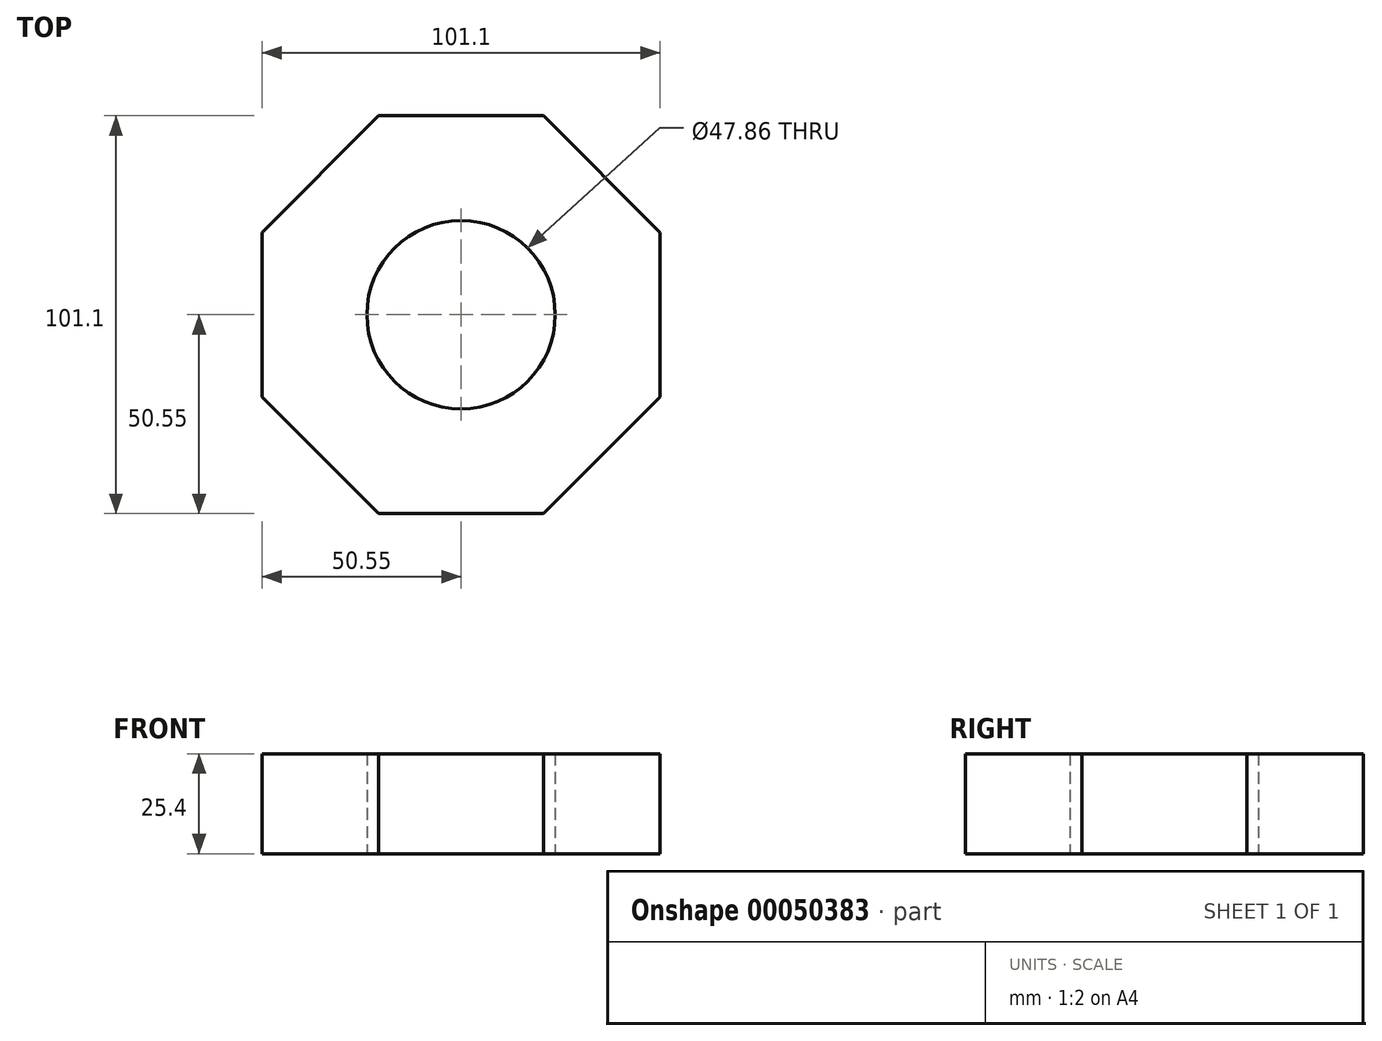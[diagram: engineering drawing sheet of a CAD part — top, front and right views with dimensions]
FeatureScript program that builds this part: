
annotation { "Feature Type Name" : "Feature", "Feature Type Description" : "" }
export const myFeature = defineFeature(function(context is Context, id is Id, definition is map)
    precondition{}
    {
        {
            var Q0;
            Q0=qCreatedBy(makeId("Top.planeOp"),FACE);
            var sketch = newSketch(context, id + "F0", { "sketchPlane" : qUnion([Q0])});
            skCircle(sketch, "E0.cCircle", {"center": v(0, 0) * mm, "radius": 50.55 * mm, "construction": true});
            skLineSegment(sketch, "E0.0", {"start": v(-50.55, -20.94) * mm, "end": v(-50.55, 20.94) * mm});
            skLineSegment(sketch, "E0.1", {"start": v(-50.55, 20.94) * mm, "end": v(-20.94, 50.55) * mm});
            skLineSegment(sketch, "E0.2", {"start": v(-20.94, 50.55) * mm, "end": v(20.94, 50.55) * mm});
            skLineSegment(sketch, "E0.3", {"start": v(20.94, 50.55) * mm, "end": v(50.55, 20.94) * mm});
            skLineSegment(sketch, "E0.4", {"start": v(50.55, 20.94) * mm, "end": v(50.55, -20.94) * mm});
            skLineSegment(sketch, "E0.5", {"start": v(50.55, -20.94) * mm, "end": v(20.94, -50.55) * mm});
            skLineSegment(sketch, "E0.6", {"start": v(20.94, -50.55) * mm, "end": v(-20.94, -50.55) * mm});
            skLineSegment(sketch, "E0.7", {"start": v(-20.94, -50.55) * mm, "end": v(-50.55, -20.94) * mm});
            skPoint(sketch, "E0.0.midPoint", {"position": v(-50.55, 0) * mm});
            skCircle(sketch, "E1", {"center": v(0, 0) * mm, "radius": 23.93 * mm});
            skSolve(sketch);
        }
        {
            var Q0;
            Q0 = qSketchRegion(id + "F0", true);
            extrude(context, id + "F1", {"entities" : qUnion([Q0]), "depth" : 25.4 * mm});
        }
    });
